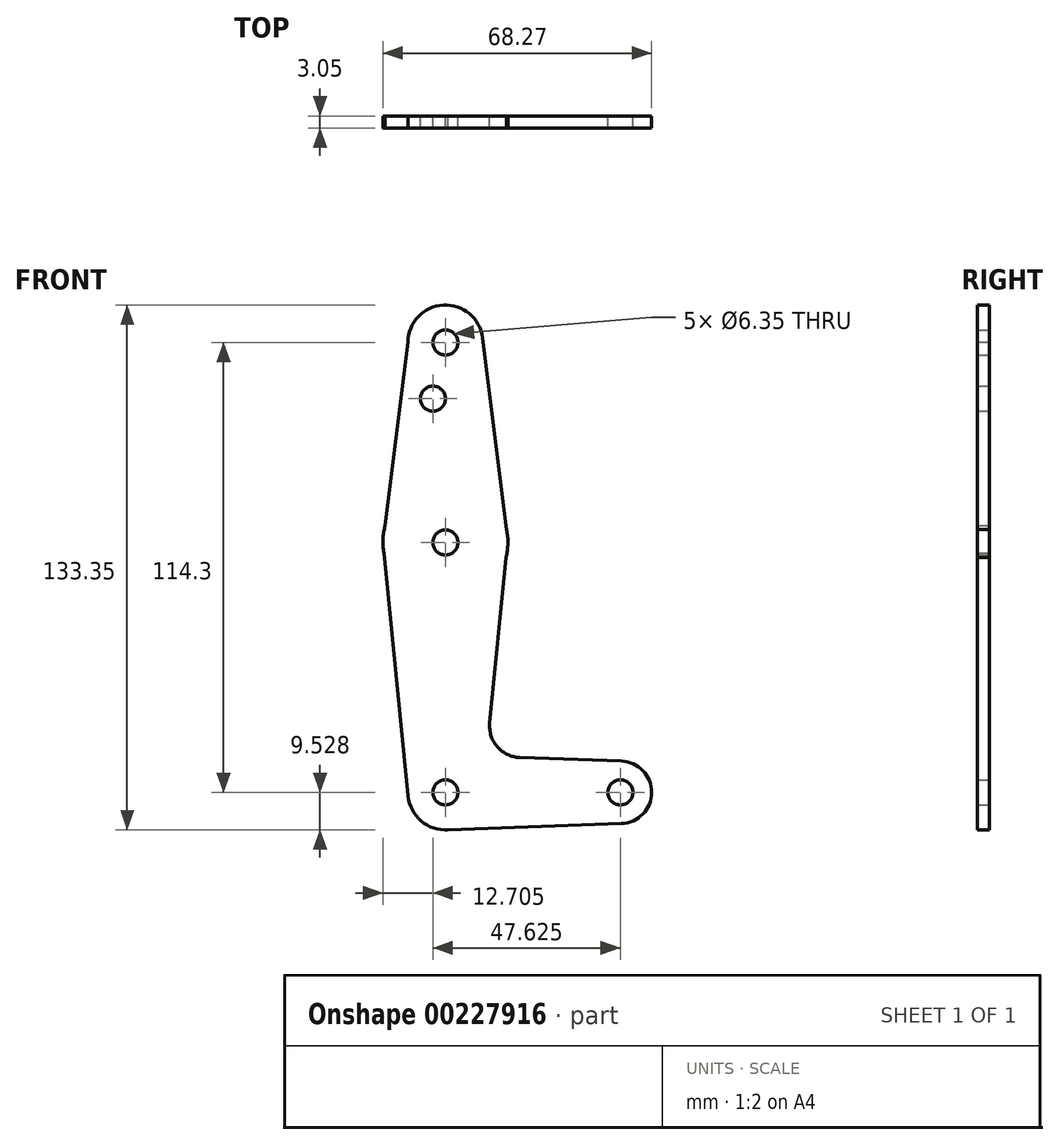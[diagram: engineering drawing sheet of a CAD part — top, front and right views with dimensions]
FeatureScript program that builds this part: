
annotation { "Feature Type Name" : "Feature", "Feature Type Description" : "" }
export const myFeature = defineFeature(function(context is Context, id is Id, definition is map)
    precondition{}
    {
        {
            var Q0;
            Q0=qCreatedBy(makeId("Front.planeOp"),FACE);
            var sketch = newSketch(context, id + "F0", { "sketchPlane" : qUnion([Q0])});
            skLineSegment(sketch, "E0", {"start": v(0, 69.46) * mm, "end": v(0, -44.84) * mm, "construction": true});
            skLineSegment(sketch, "E1", {"start": v(0, -44.84) * mm, "end": v(44.45, -44.84) * mm, "construction": true});
            skCircle(sketch, "E2", {"center": v(0, 69.46) * mm, "radius": 9.53 * mm});
            skCircle(sketch, "E3", {"center": v(0, 18.66) * mm, "radius": 15.88 * mm});
            skCircle(sketch, "E4", {"center": v(0, -44.84) * mm, "radius": 9.53 * mm});
            skCircle(sketch, "E5", {"center": v(44.45, -44.84) * mm, "radius": 7.94 * mm});
            skLineSegment(sketch, "E6", {"start": v(-9.52, 69.58) * mm, "end": v(-15.87, 18.24) * mm});
            skLineSegment(sketch, "E7", {"start": v(-15.87, 18.24) * mm, "end": v(-9.48, -45.79) * mm});
            skLineSegment(sketch, "E8", {"start": v(11.26, -27.26) * mm, "end": v(15.86, 19.33) * mm});
            skLineSegment(sketch, "E9", {"start": v(15.86, 19.33) * mm, "end": v(9.45, 70.64) * mm});
            skLineSegment(sketch, "E10", {"start": v(18.89, -35.99) * mm, "end": v(44.73, -36.9) * mm});
            skLineSegment(sketch, "E11", {"start": v(0, -54.37) * mm, "end": v(44.73, -52.77) * mm});
            skArc(sketch, "E12.filletArc", {"start": v(11.26, -27.26) * mm, "mid": v(13.19, -33.28) * mm, "end": v(18.89, -35.99) * mm});
            skCircle(sketch, "E13", {"center": v(0, 69.46) * mm, "radius": 3.18 * mm});
            skCircle(sketch, "E14", {"center": v(0, 18.66) * mm, "radius": 3.18 * mm});
            skCircle(sketch, "E15", {"center": v(0, -44.84) * mm, "radius": 3.18 * mm});
            skCircle(sketch, "E16", {"center": v(44.45, -44.84) * mm, "radius": 3.18 * mm});
            skCircle(sketch, "E17", {"center": v(-3.17, 55.18) * mm, "radius": 3.18 * mm});
            skSolve(sketch);
        }
        {
            var Q0;
            Q0 = qSketchRegion(id + "F0", true);
            extrude(context, id + "F1", {"entities" : qUnion([Q0]), "depth" : 3.05 * mm});
        }
    });
